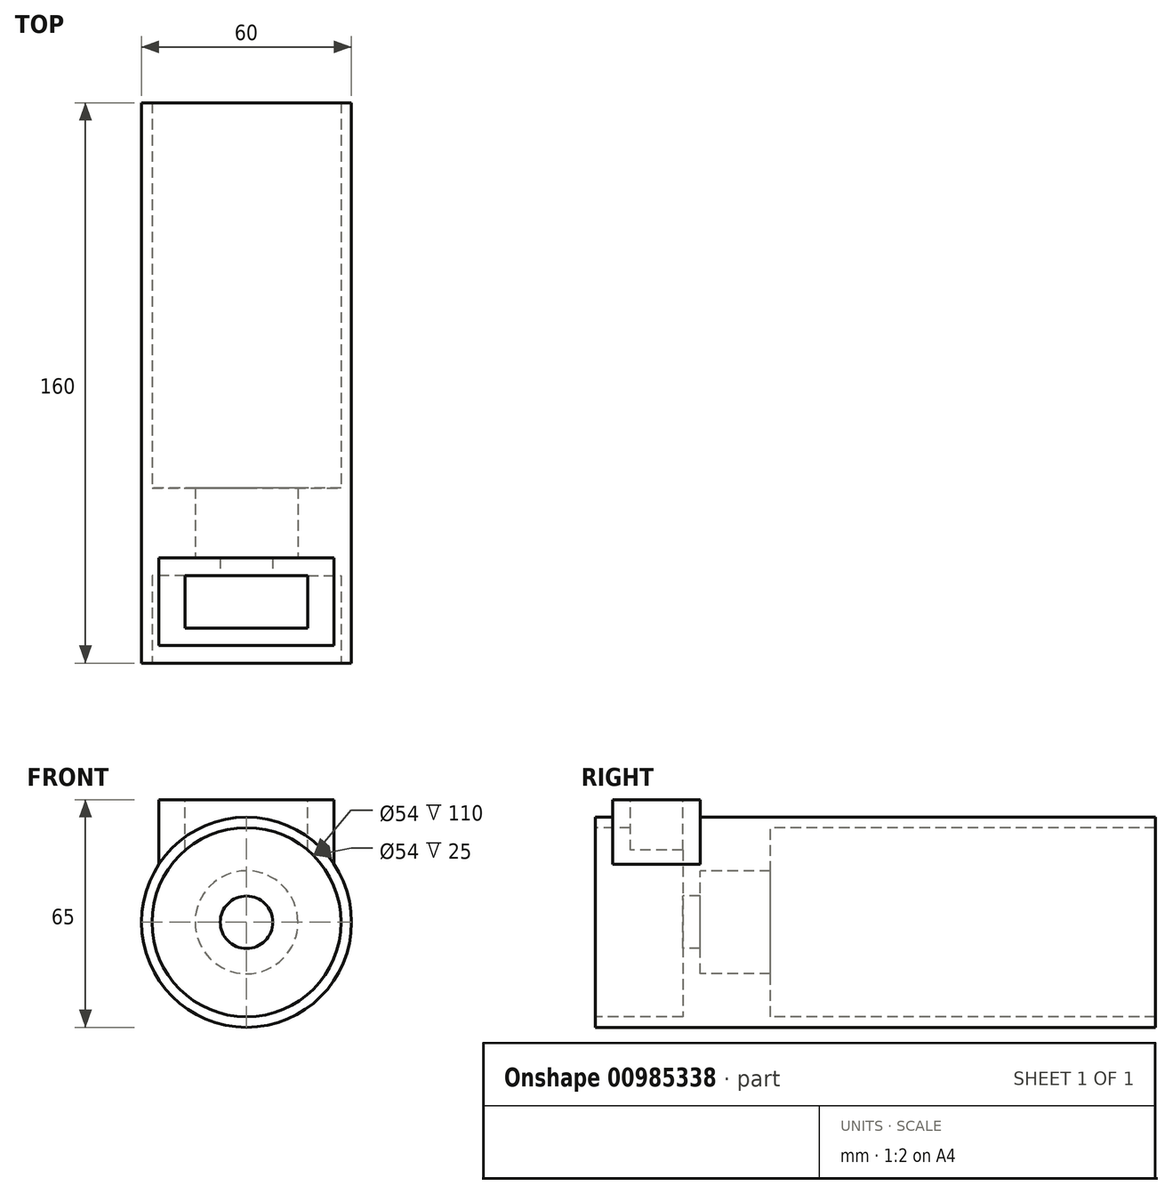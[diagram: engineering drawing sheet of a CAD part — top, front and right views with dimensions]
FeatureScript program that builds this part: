
annotation { "Feature Type Name" : "Feature", "Feature Type Description" : "" }
export const myFeature = defineFeature(function(context is Context, id is Id, definition is map)
    precondition{}
    {
        {
            var Q0;
            Q0=qCreatedBy(makeId("Front.planeOp"),FACE);
            var sketch = newSketch(context, id + "F0", { "sketchPlane" : qUnion([Q0])});
            skCircle(sketch, "E0", {"center": v(0, 0) * mm, "radius": 30 * mm});
            skCircle(sketch, "E1", {"center": v(0, 0) * mm, "radius": 27 * mm});
            skCircle(sketch, "E2", {"center": v(0, 0) * mm, "radius": 14.7 * mm});
            skCircle(sketch, "E3", {"center": v(0, 0) * mm, "radius": 7.5 * mm});
            skSolve(sketch);
        }
        {
            var Q0;
            Q0=makeQuery(id+"F0.imprint","IMPRINT",FACE,{"disambiguationData":[TD([[makeQuery(id+"F0.imprint","IMPRINT",EDGE,{"derivedFrom":sQuery(id+"F0.wireOp",EDGE,"E0")}),1.0]])]});
            extrude(context, id + "F1", {"entities" : qUnion([Q0]), "oppositeDirection" : true, "depth" : 135 * mm, "hasSecondDirection" : true, "secondDirectionOppositeDirection" : false, "secondDirectionDepth" : 25 * mm});
        }
        {
            var Q0;
            Q0=makeQuery(id+"F0.imprint","IMPRINT",FACE,{"disambiguationData":[TD([[makeQuery(id+"F0.imprint","IMPRINT",EDGE,{"derivedFrom":sQuery(id+"F0.wireOp",EDGE,"E1")}),1.0]])]});
            extrude(context, id + "F2", {"entities" : qUnion([Q0]), "operationType" : NewBodyOperationType.ADD, "oppositeDirection" : true, "depth" : 25 * mm});
        }
        {
            var Q0;
            Q0=makeQuery(id+"F0.imprint","IMPRINT",FACE,{"disambiguationData":[TD([[makeQuery(id+"F0.imprint","IMPRINT",EDGE,{"derivedFrom":sQuery(id+"F0.wireOp",EDGE,"E2")}),1.0]])]});
            extrude(context, id + "F3", {"entities" : qUnion([Q0]), "operationType" : NewBodyOperationType.ADD, "oppositeDirection" : true, "depth" : 5 * mm});
        }
        {
            var Q0;
            Q0=qCreatedBy(makeId("Front.planeOp"),FACE);
            var sketch = newSketch(context, id + "F4", { "sketchPlane" : qUnion([Q0])});
            skLineSegment(sketch, "E4", {"start": v(-25, 16.58) * mm, "end": v(-25, 35) * mm});
            skLineSegment(sketch, "E5", {"start": v(-25, 35) * mm, "end": v(25, 35) * mm});
            skLineSegment(sketch, "E6", {"start": v(25, 35) * mm, "end": v(25, 16.58) * mm});
            skArc(sketch, "E7.0", {"start": v(25, 16.58) * mm, "mid": v(0, 30) * mm, "end": v(-25, 16.58) * mm});
            skSolve(sketch);
        }
        {
            var Q0;
            Q0=qSketchRegion(id+"F4",true);
            extrude(context, id + "F5", {"entities" : qUnion([Q0]), "operationType" : NewBodyOperationType.ADD, "depth" : 20 * mm, "hasSecondDirection" : true, "secondDirectionOppositeDirection" : true, "secondDirectionDepth" : 5 * mm});
        }
        {
            var Q0;
            Q0=makeQuery(id+"F5.opExtrude","SWEPT_FACE",FACE,{"disambiguationData":[OSD([sQuery(id+"F4.wireOp",EDGE,"E5")])]});
            var sketch = newSketch(context, id + "F6", { "sketchPlane" : qUnion([Q0])});
            skLineSegment(sketch, "E8.bottom", {"start": v(-17.5, 0) * mm, "end": v(17.5, 0) * mm});
            skLineSegment(sketch, "E8.top", {"start": v(-17.5, -15) * mm, "end": v(17.5, -15) * mm});
            skLineSegment(sketch, "E8.left", {"start": v(-17.5, 0) * mm, "end": v(-17.5, -15) * mm});
            skLineSegment(sketch, "E8.right", {"start": v(17.5, 0) * mm, "end": v(17.5, -15) * mm});
            skLineSegment(sketch, "E9", {"start": v(0, 5) * mm, "end": v(0, 0) * mm});
            skSolve(sketch);
        }
        {
            var Q0;
            {var subQ1=sQuery(id+"F6.wireOp",EDGE,"E8.top");Q0=makeQuery(id+"F6.imprint","IMPRINT",FACE,{"disambiguationData":[TD([[makeQuery(id+"F6.imprint","IMPRINT",EDGE,{"derivedFrom":subQ1}),1.0]])]});}
            extrude(context, id + "F7", {"entities" : qUnion([Q0]), "operationType" : NewBodyOperationType.REMOVE, "oppositeDirection" : true, "depth" : 20 * mm});
        }
    });
